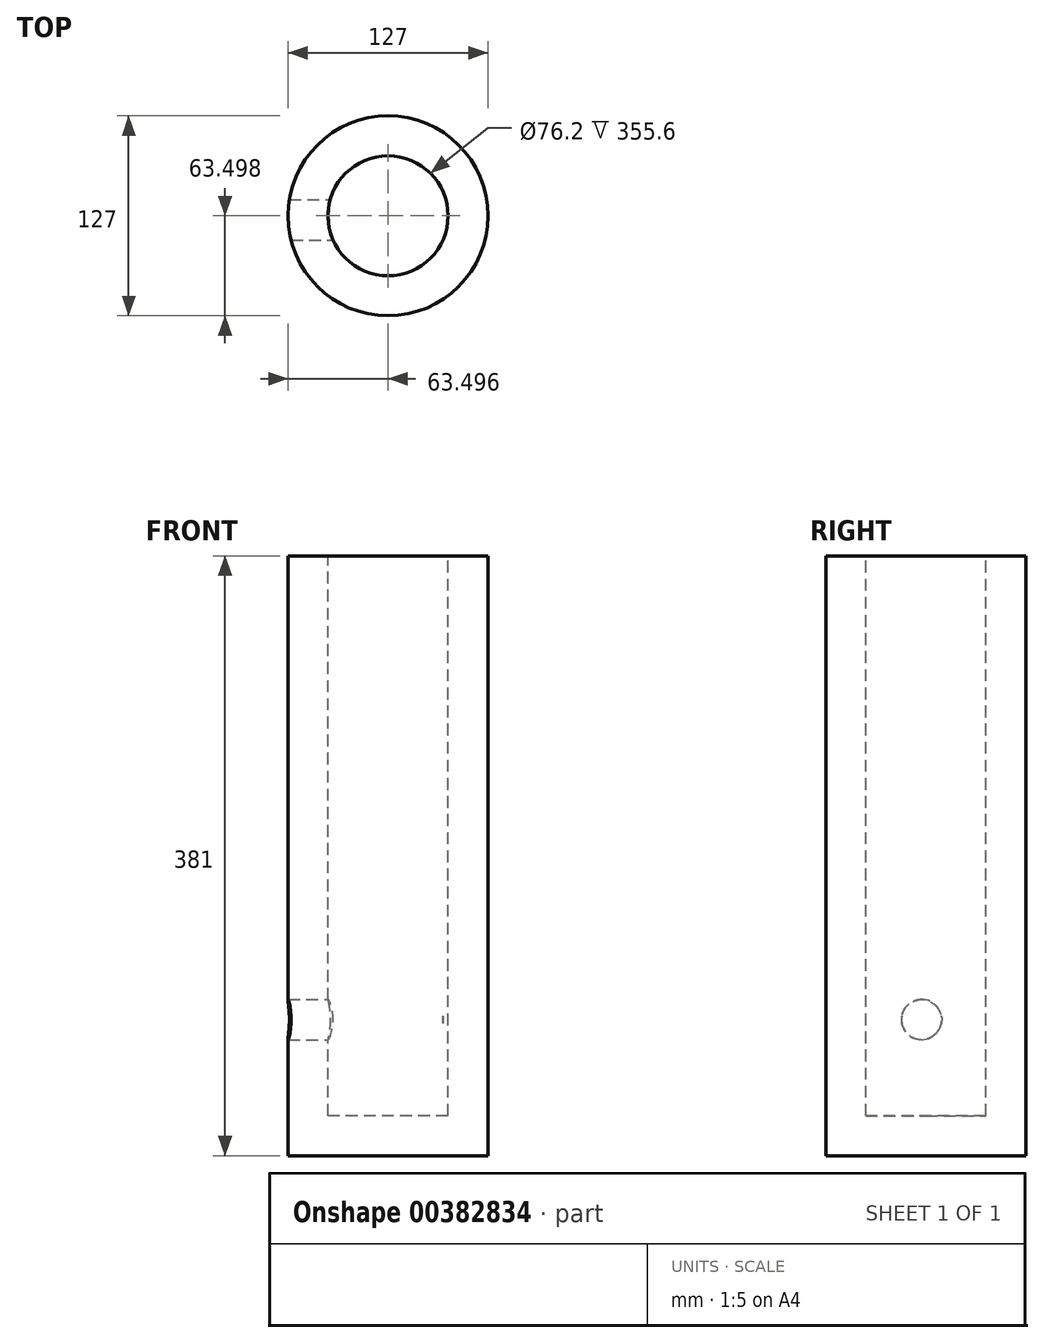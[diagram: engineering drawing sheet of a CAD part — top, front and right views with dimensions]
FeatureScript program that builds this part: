
annotation { "Feature Type Name" : "Feature", "Feature Type Description" : "" }
export const myFeature = defineFeature(function(context is Context, id is Id, definition is map)
    precondition{}
    {
        {
            var Q0;
            Q0=qCreatedBy(makeId("Top.planeOp"),FACE);
            var sketch = newSketch(context, id + "F0", { "sketchPlane" : qUnion([Q0])});
            skCircle(sketch, "E0", {"center": v(-34.94, 2.63) * mm, "radius": 63.5 * mm});
            skLineSegment(sketch, "E1", {"start": v(-98.44, 2.63) * mm, "end": v(-98.44, -10.07) * mm});
            skLineSegment(sketch, "E2", {"start": v(-98.44, 2.63) * mm, "end": v(-98.44, 15.33) * mm});
            skSolve(sketch);
        }
        {
            var Q0;
            Q0=makeQuery(id+"F0.imprint","IMPRINT",FACE,{"disambiguationData":[TD([[makeQuery(id+"F0.imprint","IMPRINT",EDGE,{"derivedFrom":sQuery(id+"F0.wireOp",EDGE,"E0")}),1.0]])]});
            extrude(context, id + "F1", {"entities" : qUnion([Q0]), "depth" : 381 * mm});
        }
        {
            var Q0;
            Q0=makeQuery(id+"F1.opExtrude","CAP_FACE",FACE,{"disambiguationData":[OSD([sQuery(id+"F0.wireOp",EDGE,"E0")])],"isStart":false});
            var sketch = newSketch(context, id + "F2", { "sketchPlane" : qUnion([Q0])});
            skCircle(sketch, "E3", {"center": v(-34.94, 2.63) * mm, "radius": 38.1 * mm});
            skSolve(sketch);
        }
        {
            var Q0;
            Q0=makeQuery(id+"F2.imprint","IMPRINT",FACE,{"disambiguationData":[TD([[makeQuery(id+"F2.imprint","IMPRINT",EDGE,{"derivedFrom":sQuery(id+"F2.wireOp",EDGE,"E3")}),1.0]])]});
            extrude(context, id + "F3", {"entities" : qUnion([Q0]), "operationType" : NewBodyOperationType.REMOVE, "oppositeDirection" : true, "depth" : 355.6 * mm});
        }
        {
            var Q0;
            Q0=qCreatedBy(makeId("Right.planeOp"),FACE);
            var sketch = newSketch(context, id + "F4", { "sketchPlane" : qUnion([Q0])});
            skCircle(sketch, "E4", {"center": v(0, 86.45) * mm, "radius": 12.78 * mm});
            skSolve(sketch);
        }
        {
            var Q0;
            Q0 = qSketchRegion(id + "F4", true);
            extrude(context, id + "F5", {"entities" : qUnion([Q0]), "operationType" : NewBodyOperationType.REMOVE, "oppositeDirection" : true, "depth" : 127 * mm});
        }
    });
